# Revit family: FU_Chair_Sandler_Varya XL 0060-PP
name_source: partatom
category: Furniture
units: mm (PartAtom-declared; Revit-internal decimal feet)

## family parameters
Always vertical = Yes
Cut with Voids When Loaded = No
OmniClass Number = 23.40.20.00
OmniClass Title = General Furniture and Specialties
Render Appearance Source = Family Geometry
Room Calculation Point = No
Shared = No
Work Plane-Based = No

## types (1)
- Varya XL 0060-PP
    Default Elevation = 0 mm  [stored 0 ft]
    Depth = 510 mm  [stored 1.67323 ft]
    Description = Swivel chair with polypropylene seat shell and 4 spoke swivel base made of cast aluminum alloy. The seat height is not adjustable. Greenguard Gold-certified to protect indoor air quality.
    Height = 850 mm  [stored 2.78871 ft]
    Manufacturer = Sandler
    Model = Varya XL 0060-PP
    URL = https://www.sandlerseating.com
    Width = 520 mm  [stored 1.70604 ft]

note: [stored X ft] marks values corroborated as IEEE doubles in the binary element streams (Revit-internal decimal feet)

## geometry (parser evidence)
native form markers: Sweep x8
no freeform markers — native parametric forms only
